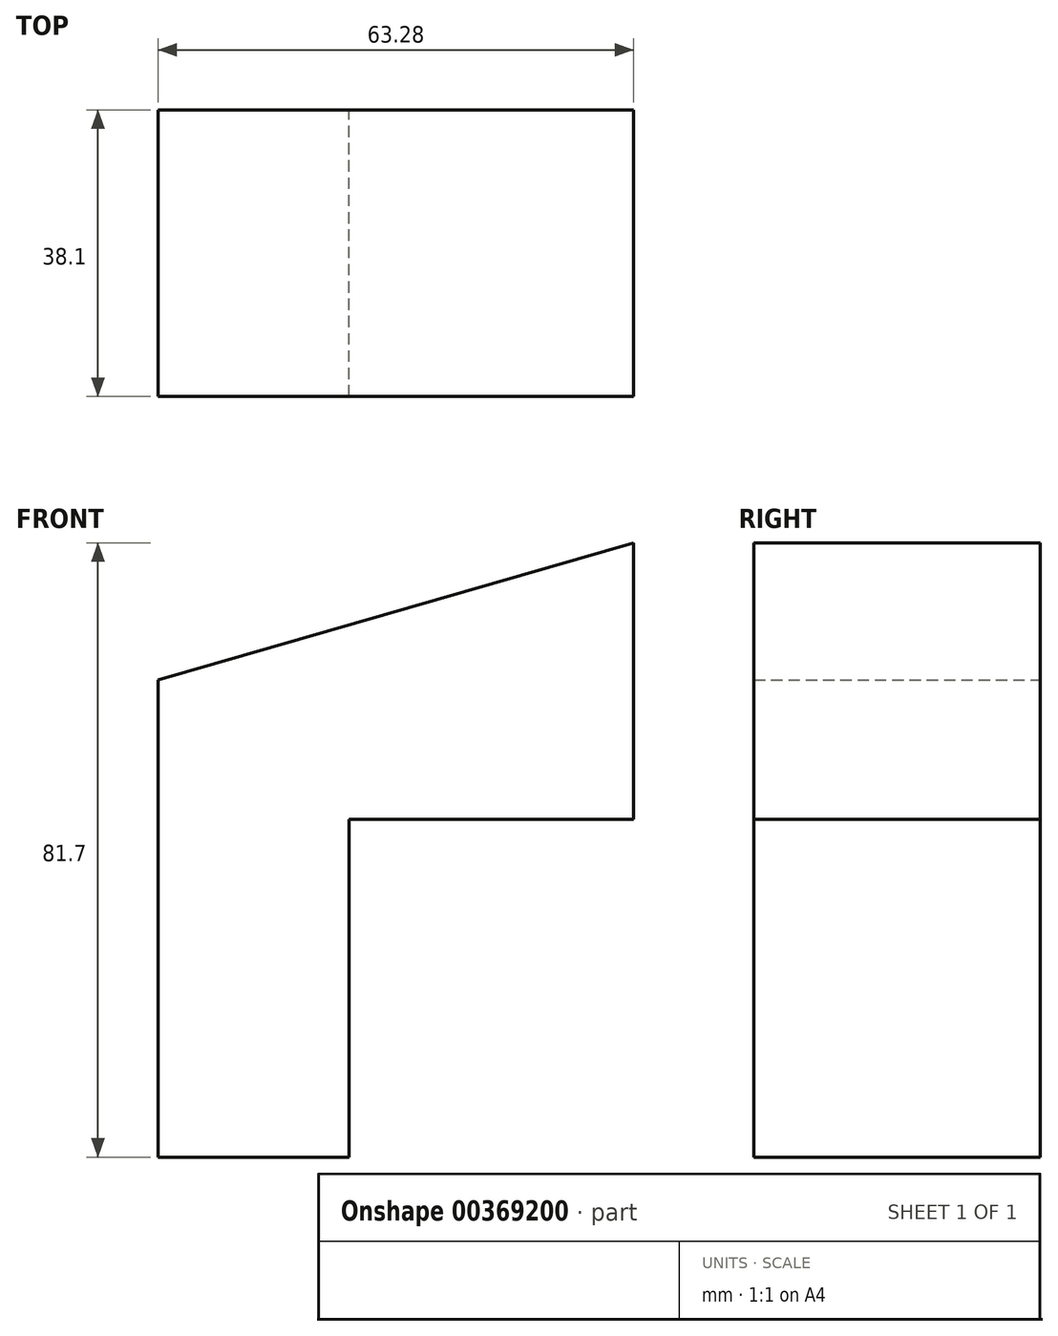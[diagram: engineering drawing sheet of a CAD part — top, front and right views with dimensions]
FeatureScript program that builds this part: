
annotation { "Feature Type Name" : "Feature", "Feature Type Description" : "" }
export const myFeature = defineFeature(function(context is Context, id is Id, definition is map)
    precondition{}
    {
        {
            var Q0;
            Q0=qCreatedBy(makeId("Front.planeOp"),FACE);
            var sketch = newSketch(context, id + "F0", { "sketchPlane" : qUnion([Q0])});
            skLineSegment(sketch, "E0", {"start": v(0, 0) * mm, "end": v(0, 63.5) * mm});
            skLineSegment(sketch, "E1", {"start": v(0, 63.5) * mm, "end": v(63.28, 81.7) * mm});
            skLineSegment(sketch, "E2", {"start": v(63.28, 81.7) * mm, "end": v(63.28, 44.96) * mm});
            skLineSegment(sketch, "E3", {"start": v(63.28, 44.96) * mm, "end": v(25.4, 44.96) * mm});
            skLineSegment(sketch, "E4", {"start": v(25.4, 44.96) * mm, "end": v(25.4, 0) * mm});
            skLineSegment(sketch, "E5", {"start": v(25.4, 0) * mm, "end": v(0, 0) * mm});
            skSolve(sketch);
        }
        {
            var Q0;
            Q0 = qSketchRegion(id + "F0", true);
            extrude(context, id + "F1", {"entities" : qUnion([Q0]), "depth" : 38.1 * mm});
        }
    });
